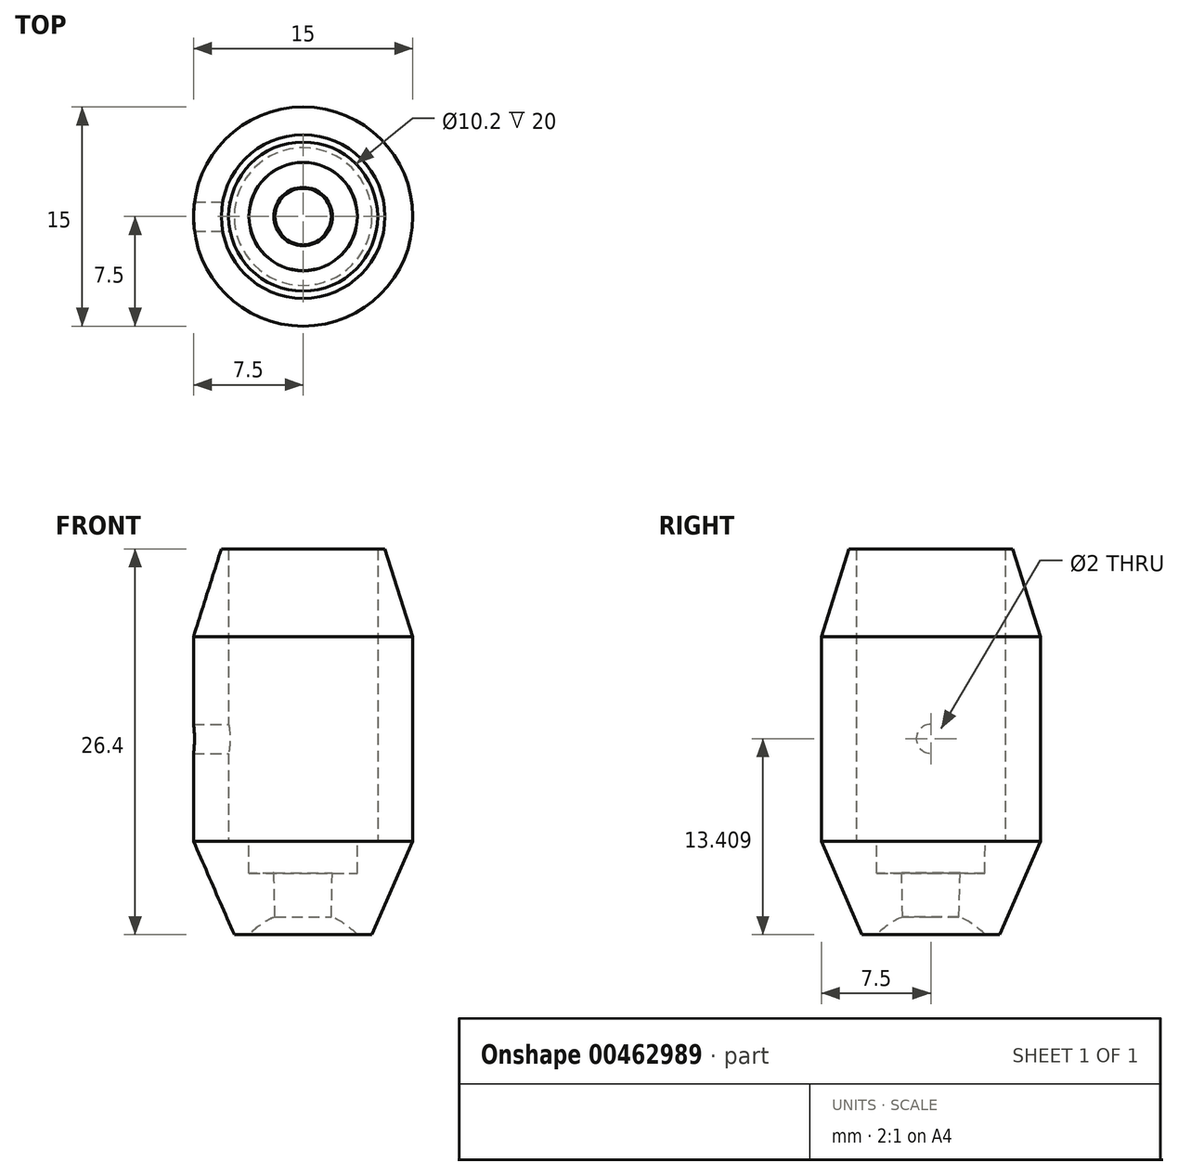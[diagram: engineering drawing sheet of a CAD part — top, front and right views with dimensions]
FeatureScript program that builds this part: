
annotation { "Feature Type Name" : "Feature", "Feature Type Description" : "" }
export const myFeature = defineFeature(function(context is Context, id is Id, definition is map)
    precondition{}
    {
        {
            var Q0;
            Q0=qCreatedBy(makeId("Front.planeOp"),FACE);
            var sketch = newSketch(context, id + "F0", { "sketchPlane" : qUnion([Q0])});
            skArc(sketch, "E0", {"start": v(-1.93, 1.22) * mm, "mid": v(-2.88, 0.7) * mm, "end": v(-3.7, 0) * mm});
            skLineSegment(sketch, "E1", {"start": v(-3.7, 0) * mm, "end": v(-4.7, 0) * mm});
            skLineSegment(sketch, "E2", {"start": v(-4.7, 0) * mm, "end": v(-7.5, 6.4) * mm});
            skLineSegment(sketch, "E3", {"start": v(-7.5, 6.4) * mm, "end": v(-7.5, 20.4) * mm});
            skLineSegment(sketch, "E4", {"start": v(-7.5, 20.4) * mm, "end": v(-5.6, 26.4) * mm});
            skLineSegment(sketch, "E5", {"start": v(-5.6, 26.4) * mm, "end": v(-5.1, 26.4) * mm});
            skLineSegment(sketch, "E6", {"start": v(-5.1, 26.4) * mm, "end": v(-5.1, 6.4) * mm});
            skLineSegment(sketch, "E7", {"start": v(-3.7, 6.4) * mm, "end": v(-3.7, 4.2) * mm});
            skLineSegment(sketch, "E8", {"start": v(-3.7, 4.2) * mm, "end": v(-2, 4.22) * mm});
            skLineSegment(sketch, "E9", {"start": v(-2, 4.22) * mm, "end": v(-1.93, 1.22) * mm});
            skLineSegment(sketch, "E10", {"start": v(-5.1, 6.4) * mm, "end": v(-3.7, 6.4) * mm});
            skLineSegment(sketch, "E11", {"start": v(0, -1.81) * mm, "end": v(0, 25.7) * mm, "construction": true});
            skSolve(sketch);
        }
        {
            var Q0;
            Q0 = qSketchRegion(id + "F0", true);
            var Q1;
            Q1=sQuery(id+"F0.wireOp",EDGE,"E11");
            revolve(context, id + "F1", {"entities" : qUnion([Q0]), "axis" : qUnion([Q1]), "revolveType" : RevolveType.FULL});
        }
        {
            var Q0;
            Q0=qCreatedBy(makeId("Right.planeOp"),FACE);
            var sketch = newSketch(context, id + "F2", { "sketchPlane" : qUnion([Q0])});
            skCircle(sketch, "E12", {"center": v(0, 13.4) * mm, "radius": 1 * mm});
            skSolve(sketch);
        }
        {
            var Q0;
            Q0 = qSketchRegion(id + "F2", true);
            extrude(context, id + "F3", {"entities" : qUnion([Q0]), "operationType" : NewBodyOperationType.REMOVE, "oppositeDirection" : true, "depth" : 8.5 * mm, "offsetDistance" : 25 * mm});
        }
    });
